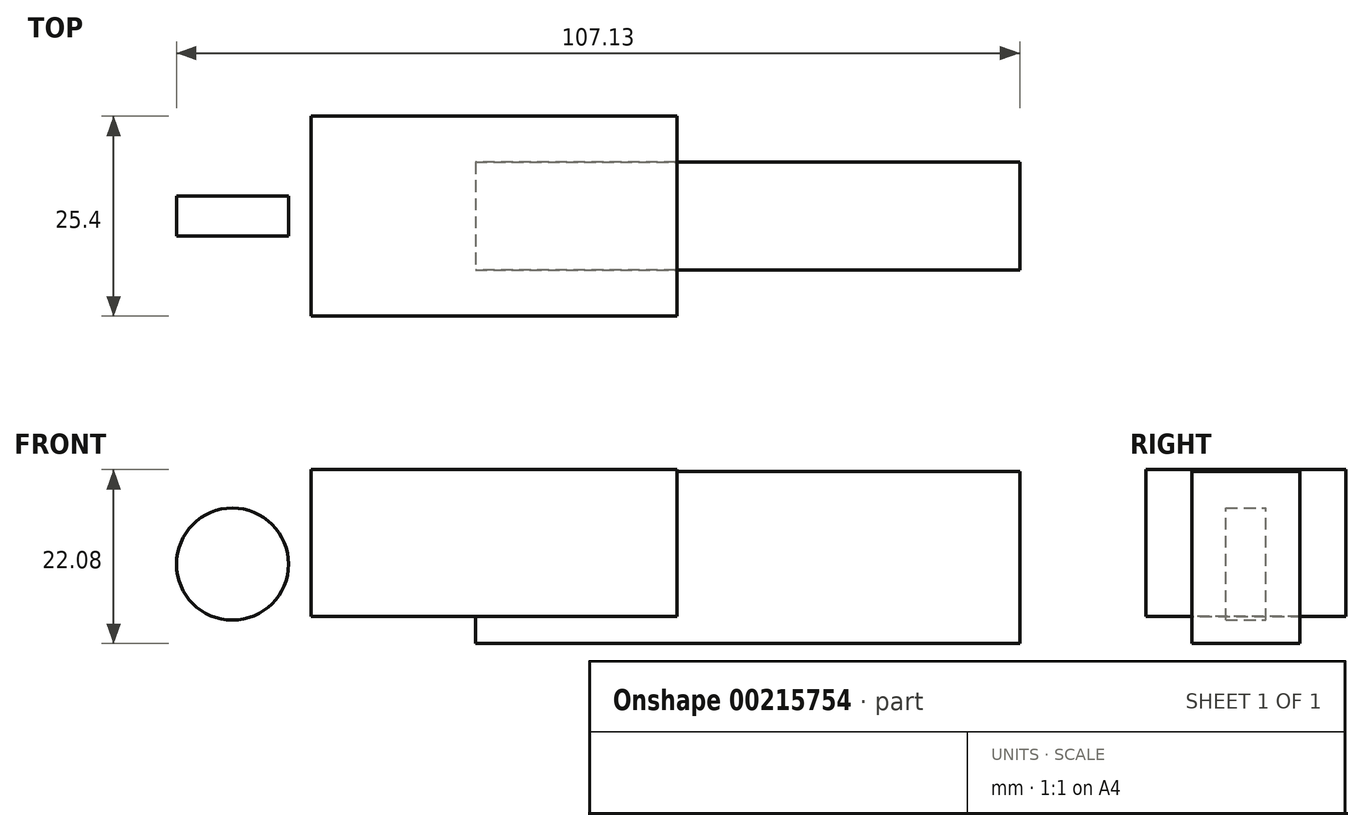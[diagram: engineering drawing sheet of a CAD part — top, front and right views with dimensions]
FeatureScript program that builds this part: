
annotation { "Feature Type Name" : "Feature", "Feature Type Description" : "" }
export const myFeature = defineFeature(function(context is Context, id is Id, definition is map)
    precondition{}
    {
        {
            var Q0;
            Q0=qCreatedBy(makeId("Front.planeOp"),FACE);
            var sketch = newSketch(context, id + "F0", { "sketchPlane" : qUnion([Q0])});
            skLineSegment(sketch, "E0.bottom", {"start": v(-90.01, -72.45) * mm, "end": v(-43.56, -72.45) * mm});
            skLineSegment(sketch, "E0.top", {"start": v(-90.01, -53.78) * mm, "end": v(-43.56, -53.78) * mm});
            skLineSegment(sketch, "E0.left", {"start": v(-90.01, -72.45) * mm, "end": v(-90.01, -53.78) * mm});
            skLineSegment(sketch, "E0.right", {"start": v(-43.56, -72.45) * mm, "end": v(-43.56, -53.78) * mm});
            skSolve(sketch);
        }
        {
            var Q0;
            Q0=qCreatedBy(makeId("Front.planeOp"),FACE);
            var sketch = newSketch(context, id + "F1", { "sketchPlane" : qUnion([Q0])});
            skCircle(sketch, "E1", {"center": v(-100.01, -65.79) * mm, "radius": 7.12 * mm});
            skSolve(sketch);
        }
        {
            var Q0;
            Q0=qCreatedBy(makeId("Front.planeOp"),FACE);
            var sketch = newSketch(context, id + "F2", { "sketchPlane" : qUnion([Q0])});
            skLineSegment(sketch, "E2.bottom", {"start": v(0, -75.86) * mm, "end": v(-69.15, -75.86) * mm});
            skLineSegment(sketch, "E2.top", {"start": v(0, -54.04) * mm, "end": v(-69.15, -54.04) * mm});
            skLineSegment(sketch, "E2.left", {"start": v(0, -75.86) * mm, "end": v(0, -54.04) * mm});
            skLineSegment(sketch, "E2.right", {"start": v(-69.15, -75.86) * mm, "end": v(-69.15, -54.04) * mm});
            skSolve(sketch);
        }
        {
            var Q0;
            Q0=makeQuery(id+"F0.imprint","IMPRINT",FACE,{"disambiguationData":[TD([[makeQuery(id+"F0.imprint","IMPRINT",EDGE,{"derivedFrom":sQuery(id+"F0.wireOp",EDGE,"E0.bottom")}),1.0]])]});
            extrude(context, id + "F3", {"entities" : qUnion([Q0]), "depth" : 12.7 * mm});
        }
        {
            var Q0;
            Q0=makeQuery(id+"F3.opExtrude","CAP_FACE",FACE,{"disambiguationData":[OSD([sQuery(id+"F0.wireOp",EDGE,"E0.bottom"),sQuery(id+"F0.wireOp",EDGE,"E0.top"),sQuery(id+"F0.wireOp",EDGE,"E0.left"),sQuery(id+"F0.wireOp",EDGE,"E0.right")])],"isStart":true});
            extrude(context, id + "F4", {"entities" : qUnion([Q0]), "operationType" : NewBodyOperationType.ADD, "depth" : 12.7 * mm});
        }
        {
            var Q0;
            Q0=makeQuery(id+"F1.imprint","IMPRINT",FACE,{"disambiguationData":[TD([[makeQuery(id+"F1.imprint","IMPRINT",EDGE,{"derivedFrom":sQuery(id+"F1.wireOp",EDGE,"E1")}),1.0]])]});
            extrude(context, id + "F5", {"entities" : qUnion([Q0]), "depth" : 2.54 * mm});
        }
        {
            var Q0;
            Q0=makeQuery(id+"F5.opExtrude","CAP_FACE",FACE,{"disambiguationData":[OSD([sQuery(id+"F1.wireOp",EDGE,"E1")])],"isStart":true});
            extrude(context, id + "F6", {"entities" : qUnion([Q0]), "operationType" : NewBodyOperationType.ADD, "depth" : 2.54 * mm});
        }
        {
            var Q0;
            Q0=makeQuery(id+"F2.imprint","IMPRINT",FACE,{"disambiguationData":[TD([[makeQuery(id+"F2.imprint","IMPRINT",EDGE,{"derivedFrom":sQuery(id+"F2.wireOp",EDGE,"E2.bottom")}),-1.0]])]});
            extrude(context, id + "F7", {"entities" : qUnion([Q0]), "operationType" : NewBodyOperationType.ADD, "depth" : 6.86 * mm});
        }
        {
            var Q0;
            Q0=makeQuery(id+"F7.opExtrude","CAP_FACE",FACE,{"disambiguationData":[OSD([sQuery(id+"F2.wireOp",EDGE,"E2.bottom"),sQuery(id+"F2.wireOp",EDGE,"E2.top"),sQuery(id+"F2.wireOp",EDGE,"E2.left"),sQuery(id+"F2.wireOp",EDGE,"E2.right")])],"isStart":true});
            extrude(context, id + "F8", {"entities" : qUnion([Q0]), "operationType" : NewBodyOperationType.ADD, "depth" : 6.86 * mm});
        }
        {
            var Q0;
            Q0=qCreatedBy(makeId("Front.planeOp"),FACE);
            var sketch = newSketch(context, id + "F9", { "sketchPlane" : qUnion([Q0])});
            skCircle(sketch, "E3", {"center": v(-78.53, -73.73) * mm, "radius": 3.43 * mm});
            skSolve(sketch);
        }
        {
            var Q0;
            Q0=sQuery(id+"F9.wireOp",EDGE,"E3");
            extrude(context, id + "F10", {"bodyType" : ToolBodyType.SURFACE, "surfaceEntities" : qUnion([Q0]), "depth" : 6.86 * mm});
        }
        {
            var Q0;
            Q0=sQuery(id+"F9.wireOp",EDGE,"E3");
            extrude(context, id + "F11", {"bodyType" : ToolBodyType.SURFACE, "surfaceEntities" : qUnion([Q0]), "endBound" : BoundingType.SYMMETRIC, "depth" : 25.4 * mm});
        }
    });
